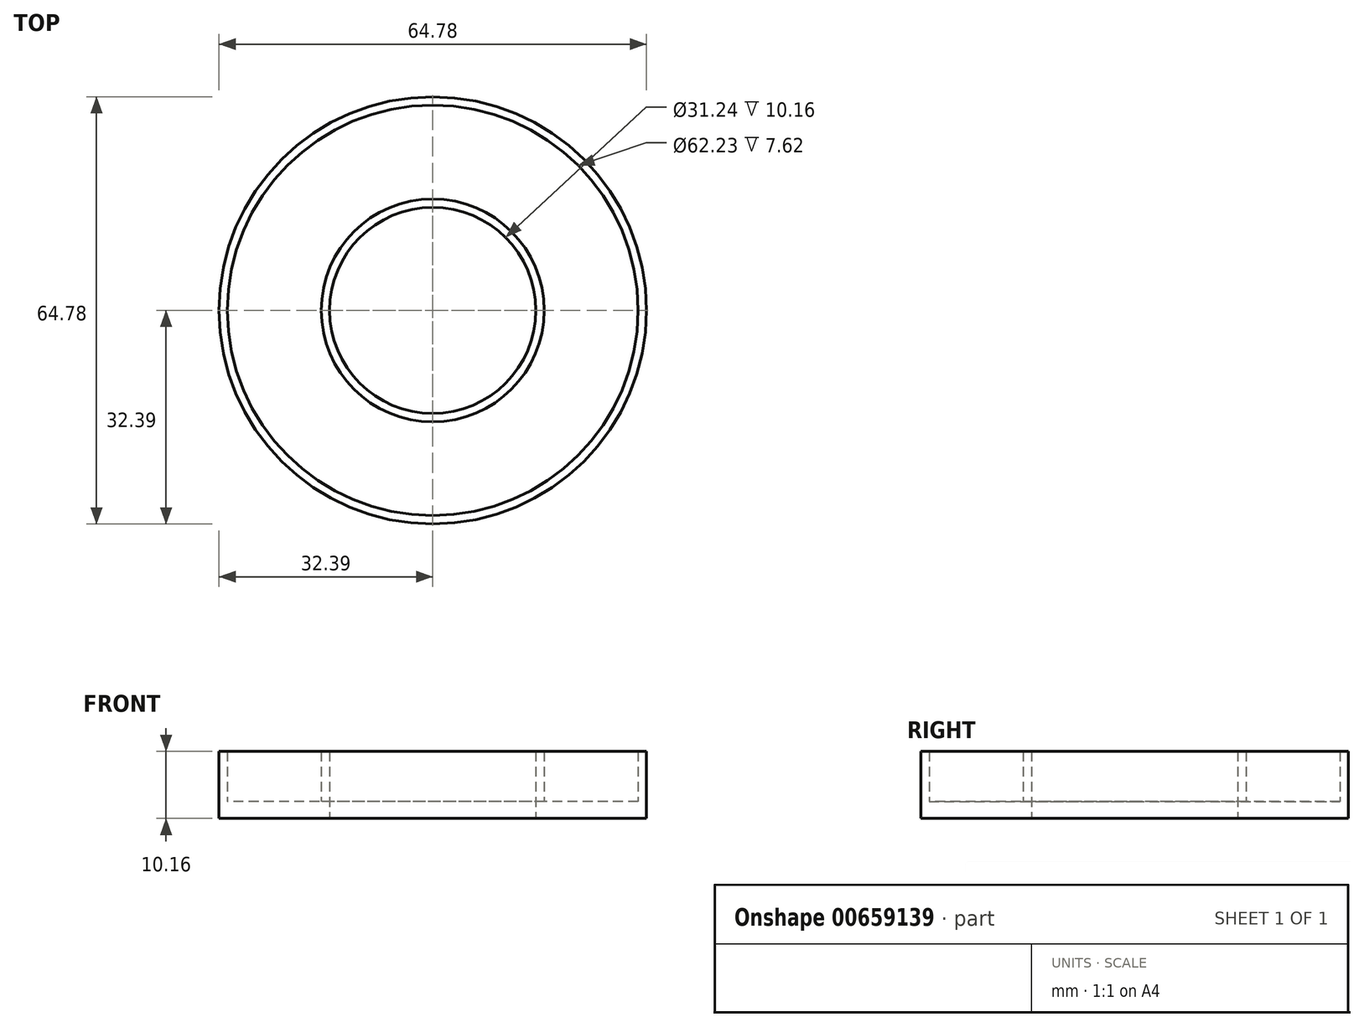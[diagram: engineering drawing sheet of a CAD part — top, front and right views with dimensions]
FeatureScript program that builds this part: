
annotation { "Feature Type Name" : "Feature", "Feature Type Description" : "" }
export const myFeature = defineFeature(function(context is Context, id is Id, definition is map)
    precondition{}
    {
        {
            var Q0;
            Q0=qCreatedBy(makeId("Top.planeOp"),FACE);
            var sketch = newSketch(context, id + "F0", { "sketchPlane" : qUnion([Q0])});
            skCircle(sketch, "E0", {"center": v(0, 0) * mm, "radius": 15.62 * mm});
            skCircle(sketch, "E1", {"center": v(0, 0) * mm, "radius": 32.39 * mm});
            skSolve(sketch);
        }
        {
            var Q0;
            Q0=makeQuery(id+"F0.imprint","IMPRINT",FACE,{"disambiguationData":[TD([[makeQuery(id+"F0.imprint","IMPRINT",EDGE,{"derivedFrom":sQuery(id+"F0.wireOp",EDGE,"E0")}),-1.0]])]});
            extrude(context, id + "F1", {"entities" : qUnion([Q0]), "depth" : 2.54 * mm, "offsetDistance" : 25.4 * mm});
        }
        {
            var Q0;
            Q0=qCreatedBy(makeId("Top.planeOp"),FACE);
            var sketch = newSketch(context, id + "F2", { "sketchPlane" : qUnion([Q0])});
            skCircle(sketch, "E2", {"center": v(0, 0) * mm, "radius": 31.12 * mm});
            skCircle(sketch, "E3", {"center": v(0, 0) * mm, "radius": 32.39 * mm});
            skSolve(sketch);
        }
        {
            var Q0;
            Q0 = qSketchRegion(id + "F2", true);
            extrude(context, id + "F3", {"entities" : qUnion([Q0]), "operationType" : NewBodyOperationType.ADD, "depth" : 10.16 * mm, "offsetDistance" : 25.4 * mm});
        }
        {
            var Q0;
            Q0=qCreatedBy(makeId("Top.planeOp"),FACE);
            var sketch = newSketch(context, id + "F4", { "sketchPlane" : qUnion([Q0])});
            skCircle(sketch, "E4", {"center": v(0, 0) * mm, "radius": 16.9 * mm});
            skCircle(sketch, "E5", {"center": v(0, 0) * mm, "radius": 15.62 * mm});
            skSolve(sketch);
        }
        {
            var Q0;
            Q0 = qSketchRegion(id + "F4", true);
            extrude(context, id + "F5", {"entities" : qUnion([Q0]), "operationType" : NewBodyOperationType.ADD, "depth" : 10.16 * mm, "offsetDistance" : 25.4 * mm});
        }
    });
